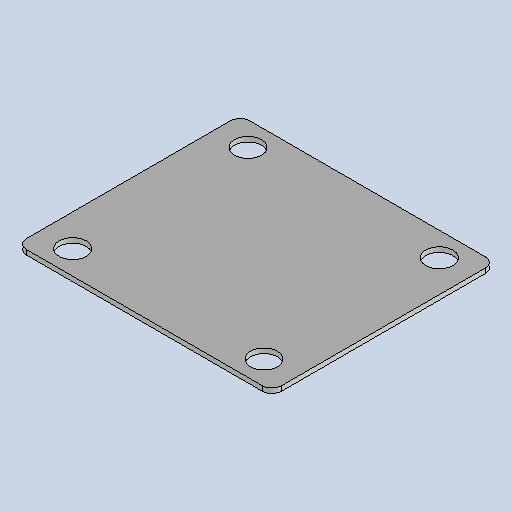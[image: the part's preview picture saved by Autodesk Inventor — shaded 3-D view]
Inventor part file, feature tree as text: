
AUTODESK INVENTOR PART (.ipt)
format: ipt  version: 2025 (Build 290162010, 162A)  size: 121,856 bytes
history: native  units: mm
features: sketch x2, sheet_metal_op x1, chamfer x1, other x1
ambient origin geometry x8: Origin, YZ Plane, XZ Plane, XY Plane, X Axis, Y Axis, Z Axis, Center Point
bodies: Solid1 (feature_tree)
feature tree (5):
  sketch  "3D Sketch1"
  sheet_metal_op  "Face1"
  chamfer  "Corner Round1"
  sketch  "Sketch1"  dims[d0=50.0mm d1=23.865632mm d2=8.726646mm d6=3.0mm d30=140.0mm d34=160.0mm d35=17.0mm d36=20.0mm d37=15.0mm d38=6.0mm]
  other  "Plate1"
